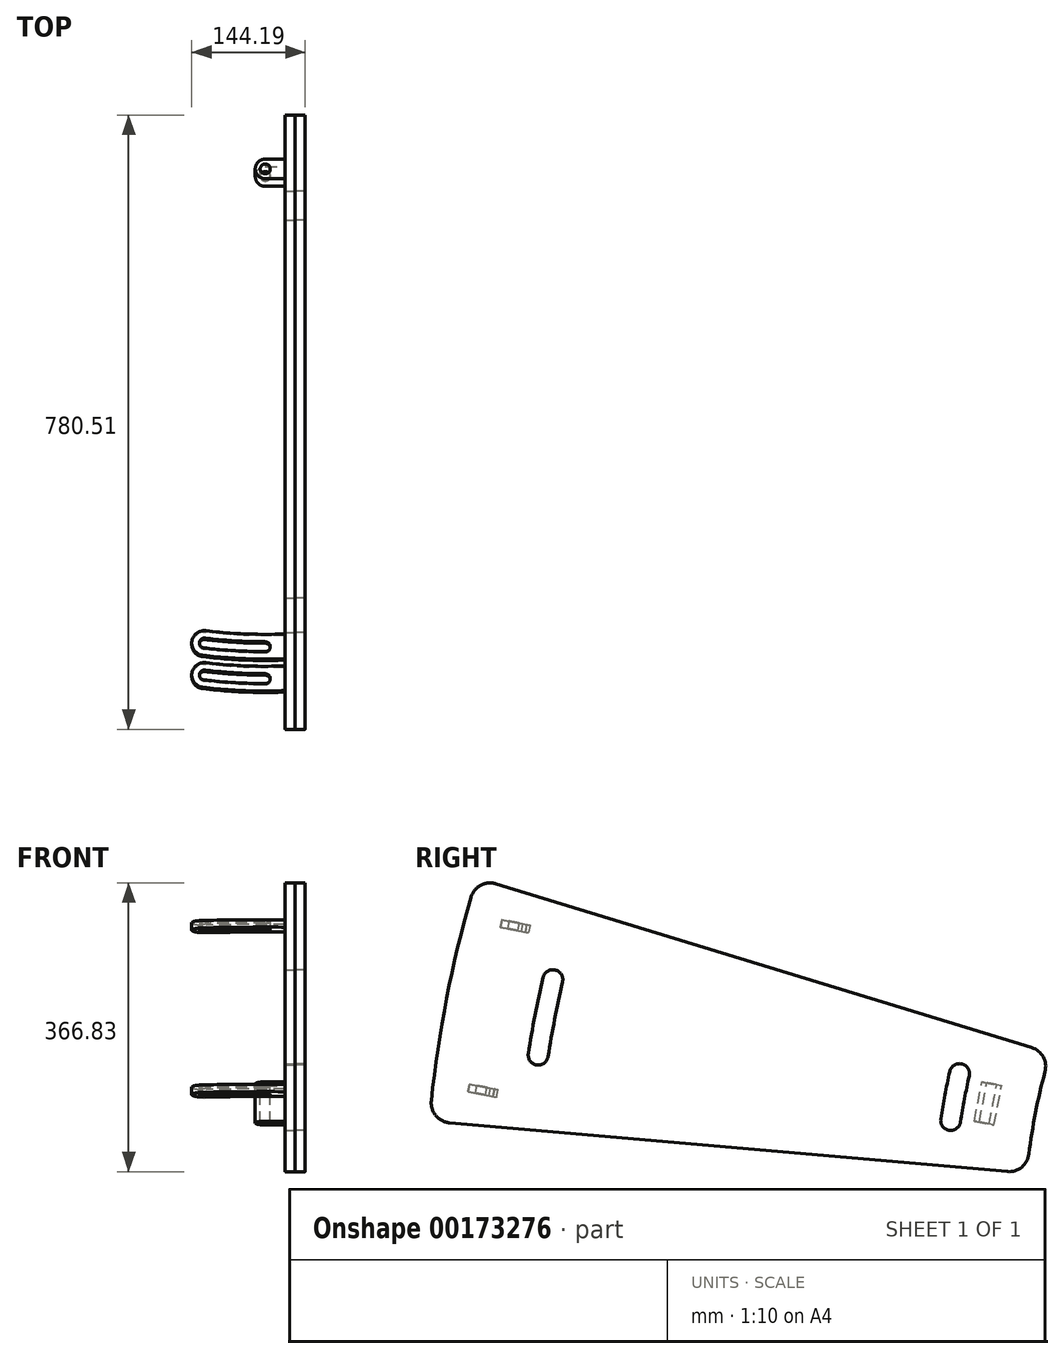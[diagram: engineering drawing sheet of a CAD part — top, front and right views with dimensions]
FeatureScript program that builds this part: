
annotation { "Feature Type Name" : "Feature", "Feature Type Description" : "" }
export const myFeature = defineFeature(function(context is Context, id is Id, definition is map)
    precondition{}
    {
        {
            var Q0;
            Q0=qCreatedBy(makeId("Right.planeOp"),FACE);
            var sketch = newSketch(context, id + "F0", { "sketchPlane" : qUnion([Q0])});
            skArc(sketch, "E0", {"start": v(-736.01, 197.3) * mm, "mid": v(-748, 145.4) * mm, "end": v(-756.33, 92.77) * mm});
            skLineSegment(sketch, "E1", {"start": v(0, 0) * mm, "end": v(-6.79, 0) * mm, "construction": true});
            skLineSegment(sketch, "E2", {"start": v(0, 0) * mm, "end": v(-1486.5, 288.95) * mm, "construction": true});
            skArc(sketch, "E3", {"start": v(-1465.3, 418.87) * mm, "mid": v(-1496, 290.8) * mm, "end": v(-1515.52, 160.55) * mm});
            skLineSegment(sketch, "E4", {"start": v(22.77, 0) * mm, "end": v(-18.63, 3.62) * mm});
            skArc(sketch, "E5", {"start": v(-844.59, 194.99) * mm, "mid": v(-850.72, 165.37) * mm, "end": v(-855.84, 135.55) * mm, "construction": true});
            skArc(sketch, "E6", {"start": v(-1361.2, 314.26) * mm, "mid": v(-1371.33, 266.56) * mm, "end": v(-1379.8, 218.54) * mm, "construction": true});
            skLineSegment(sketch, "E7.MirrorCS", {"start": v(21.1, -8.53) * mm, "end": v(-18.63, 3.62) * mm});
            skLineSegment(sketch, "E8.trimOffspring", {"start": v(-753.12, 228.18) * mm, "end": v(-1433.46, 436.18) * mm});
            skLineSegment(sketch, "E9.trimOffspring", {"start": v(-783.76, 70.56) * mm, "end": v(-1492.48, 132.57) * mm});
            skLineSegment(sketch, "E10.trimOffspring", {"start": v(-762, 0) * mm, "end": v(-1563.5, 0) * mm, "construction": true});
            skPoint(sketch, "E11.orphan", {"position": v(-1640.89, 499.6) * mm});
            skLineSegment(sketch, "E12", {"start": v(0, 0) * mm, "end": v(-1555.73, 246.4) * mm, "construction": true});
            skLineSegment(sketch, "E13", {"start": v(0, 0) * mm, "end": v(0, 0) * mm});
            skLineSegment(sketch, "E14.MirrorCS", {"start": v(0, 0) * mm, "end": v(-1534.75, 354.33) * mm, "construction": true});
            skArc(sketch, "E15.trimOffspring", {"start": v(-862.85, 77.48) * mm, "mid": v(-865.39, 38.78) * mm, "end": v(-866.23, 0) * mm, "construction": true});
            skArc(sketch, "E16.trimOffspring", {"start": v(-1391.5, 123.73) * mm, "mid": v(1371.33, -266.56) * mm, "end": v(-1336.54, 406.55) * mm, "construction": true});
            skArc(sketch, "E17.0.startCap", {"start": v(-1373.57, 317.11) * mm, "mid": v(-1358.34, 326.63) * mm, "end": v(-1348.82, 311.4) * mm});
            skArc(sketch, "E17.0.endCap", {"start": v(-1367.26, 216.55) * mm, "mid": v(-1381.79, 206) * mm, "end": v(-1392.34, 220.53) * mm});
            skArc(sketch, "E17.0.left", {"start": v(-1348.82, 311.4) * mm, "mid": v(-1358.87, 264.14) * mm, "end": v(-1367.26, 216.55) * mm});
            skArc(sketch, "E17.0.right", {"start": v(-1373.57, 317.11) * mm, "mid": v(-1383.8, 268.98) * mm, "end": v(-1392.34, 220.53) * mm});
            skArc(sketch, "E18.0.startCap", {"start": v(-856.98, 197.77) * mm, "mid": v(-841.8, 207.38) * mm, "end": v(-832.2, 192.2) * mm});
            skArc(sketch, "E18.0.endCap", {"start": v(-843.29, 133.62) * mm, "mid": v(-857.78, 123) * mm, "end": v(-868.4, 137.49) * mm});
            skArc(sketch, "E18.0.left", {"start": v(-832.2, 192.2) * mm, "mid": v(-838.24, 163) * mm, "end": v(-843.29, 133.62) * mm});
            skArc(sketch, "E18.0.right", {"start": v(-856.98, 197.77) * mm, "mid": v(-863.2, 167.73) * mm, "end": v(-868.4, 137.49) * mm});
            skPoint(sketch, "E19.visualSharp", {"position": v(-1457.99, 443.68) * mm});
            skArc(sketch, "E19.filletArc", {"start": v(-1433.46, 436.18) * mm, "mid": v(-1453.01, 434.2) * mm, "end": v(-1465.3, 418.87) * mm});
            skPoint(sketch, "E20.visualSharp", {"position": v(-729.28, 220.89) * mm});
            skArc(sketch, "E20.filletArc", {"start": v(-736.01, 197.3) * mm, "mid": v(-738.33, 216.2) * mm, "end": v(-753.12, 228.18) * mm});
            skPoint(sketch, "E21.visualSharp", {"position": v(-758.92, 68.39) * mm});
            skArc(sketch, "E21.filletArc", {"start": v(-783.76, 70.56) * mm, "mid": v(-765.56, 76.13) * mm, "end": v(-756.33, 92.77) * mm});
            skPoint(sketch, "E22.newPointA", {"position": v(-1708.56, 151.47) * mm});
            skArc(sketch, "E22.filletArc", {"start": v(-1515.52, 160.55) * mm, "mid": v(-1509.87, 141.72) * mm, "end": v(-1492.48, 132.57) * mm});
            skSolve(sketch);
        }
        {
            var Q0;
            Q0=makeQuery(id+"F0.imprint","IMPRINT",FACE,{"disambiguationData":[TD([[makeQuery(id+"F0.imprint","IMPRINT",EDGE,{"derivedFrom":sQuery(id+"F0.wireOp",EDGE,"E0")}),-1.0]])]});
            var Q1;
            Q1=makeQuery(id+"F0.imprint","IMPRINT",FACE,{"disambiguationData":[TD([[makeQuery(id+"F0.imprint","IMPRINT",EDGE,{"derivedFrom":sQuery(id+"F0.wireOp",EDGE,"E17.0.startCap")}),-1.0]])]});
            var Q2;
            Q2=makeQuery(id+"F0.imprint","IMPRINT",FACE,{"disambiguationData":[TD([[makeQuery(id+"F0.imprint","IMPRINT",EDGE,{"derivedFrom":sQuery(id+"F0.wireOp",EDGE,"E18.0.startCap")}),-1.0]])]});
            extrude(context, id + "F1", {"entities" : qUnion([Q0, Q1, Q2]), "oppositeDirection" : true, "depth" : 12.7 * mm});
        }
        {
            var Q0;
            Q0=makeQuery(id+"F0.imprint","IMPRINT",FACE,{"disambiguationData":[TD([[makeQuery(id+"F0.imprint","IMPRINT",EDGE,{"derivedFrom":sQuery(id+"F0.wireOp",EDGE,"E17.0.startCap")}),-1.0]])]});
            var Q1;
            Q1=makeQuery(id+"F0.imprint","IMPRINT",FACE,{"disambiguationData":[TD([[makeQuery(id+"F0.imprint","IMPRINT",EDGE,{"derivedFrom":sQuery(id+"F0.wireOp",EDGE,"E18.0.startCap")}),-1.0]])]});
            extrude(context, id + "F2", {"entities" : qUnion([Q0, Q1]), "depth" : 12.7 * mm});
        }
        {
            var Q0;
            Q0=makeQuery(id+"F2.opExtrude","CAP_FACE",FACE,{"disambiguationData":[OSD([sQuery(id+"F0.wireOp",EDGE,"E17.0.startCap"),sQuery(id+"F0.wireOp",EDGE,"E17.0.endCap"),sQuery(id+"F0.wireOp",EDGE,"E17.0.left"),sQuery(id+"F0.wireOp",EDGE,"E17.0.right")])],"isStart":false});
            var sketch = newSketch(context, id + "F3", { "sketchPlane" : qUnion([Q0])});
            skPoint(sketch, "E23", {"position": v(-1361.2, 314.26) * mm});
            skPoint(sketch, "E24", {"position": v(-1379.8, 218.54) * mm});
            skArc(sketch, "E25.0.0", {"start": v(-832.2, 192.2) * mm, "mid": v(-841.8, 207.38) * mm, "end": v(-856.98, 197.77) * mm, "construction": true});
            skArc(sketch, "E25.0.1", {"start": v(-856.98, 197.77) * mm, "mid": v(-863.2, 167.73) * mm, "end": v(-868.4, 137.49) * mm, "construction": true});
            skArc(sketch, "E25.0.2", {"start": v(-868.4, 137.49) * mm, "mid": v(-857.78, 123) * mm, "end": v(-843.29, 133.62) * mm, "construction": true});
            skArc(sketch, "E25.0.3", {"start": v(-843.29, 133.62) * mm, "mid": v(-838.24, 163) * mm, "end": v(-832.2, 192.2) * mm, "construction": true});
            skSolve(sketch);
        }
        {
            var Q0;
            Q0=sQuery(id+"F3.wireOp",VERTEX,"E23");
            var Q1;
            Q1=sQuery(id+"F3.wireOp",VERTEX,"E24");
            var Q2;
            Q2=sQuery(id+"F3.wireOp",VERTEX,"E25.0.0.center");
            var Q3;
            Q3=sQuery(id+"F3.wireOp",VERTEX,"E25.0.2.center");
            var Q4;
            Q4=makeQuery(id+"F1.opExtrude","SWEPT_BODY",BODY,{"disambiguationData":[OSD([sQuery(id+"F0.wireOp",EDGE,"E0"),sQuery(id+"F0.wireOp",EDGE,"E3"),sQuery(id+"F0.wireOp",EDGE,"E8.trimOffspring"),sQuery(id+"F0.wireOp",EDGE,"E9.trimOffspring"),sQuery(id+"F0.wireOp",EDGE,"E19.filletArc"),sQuery(id+"F0.wireOp",EDGE,"E20.filletArc"),sQuery(id+"F0.wireOp",EDGE,"E21.filletArc"),sQuery(id+"F0.wireOp",EDGE,"E22.filletArc")])]});
            hole(context, id + "F4", {"style" : HoleStyle.SIMPLE, "endStyle" : HoleEndStyle.THROUGH, "standardTappedOrClearance" : lookupTablePath({ "standard" : "ANSI", "fit" : "Normal (ASME)", "size" : "5/8", "type" : "Clearance" }), "standardBlindInLast" : lookupTablePath({ "fit" : "Free", "standard" : "ANSI", "size" : "5/8", "type" : "Clearance" }), "holeDiameter" : 16.67 * mm, "locations" : qUnion([Q0, Q1, Q2, Q3]), "scope" : qUnion([Q4]), "isTappedThrough" : true});
        }
        {
            var Q0;
            Q0=makeQuery(id+"F1.opExtrude","SWEPT_FACE",FACE,{"disambiguationData":[OSD([sQuery(id+"F0.wireOp",EDGE,"E9.trimOffspring")])]});
            var Q1;
            Q1=makeQuery(id+"F1.opExtrude","SWEPT_FACE",FACE,{"disambiguationData":[OSD([sQuery(id+"F0.wireOp",EDGE,"E8.trimOffspring")])]});
            cPlane(context, id + "F5", {"entities" : qUnion([Q0, Q1]), "cplaneType" : CPlaneType.MID_PLANE, "offset" : 25.4 * mm, "width" : 152.4 * mm, "height" : 152.4 * mm});
        }
        {
            var Q0;
            Q0=qCreatedBy(id+"F5.planeOp",FACE);
            var sketch = newSketch(context, id + "F6", { "sketchPlane" : qUnion([Q0])});
            skLineSegment(sketch, "E26.0", {"start": v(-12.7, 782.82) * mm, "end": v(-12.7, 1490.35) * mm, "construction": true});
            skLineSegment(sketch, "E27", {"start": v(0, 760.08) * mm, "end": v(-12.7, 760.08) * mm, "construction": true});
            skLineSegment(sketch, "E28", {"start": v(-12.7, 760.08) * mm, "end": v(-65.49, 760.08) * mm, "construction": true});
            skLineSegment(sketch, "E29.0", {"start": v(-12.7, 823.58) * mm, "end": v(-38.1, 823.58) * mm, "construction": true});
            skCircle(sketch, "E30", {"center": v(-38.1, 823.58) * mm, "radius": 6.35 * mm});
            skCircle(sketch, "E31", {"center": v(-38.1, 823.58) * mm, "radius": 12.7 * mm});
            skLineSegment(sketch, "E32", {"start": v(-38.1, 829.93) * mm, "end": v(-38.1, 836.28) * mm});
            skLineSegment(sketch, "E33", {"start": v(-38.1, 836.28) * mm, "end": v(-12.7, 836.28) * mm});
            skLineSegment(sketch, "E34", {"start": v(-38.1, 817.23) * mm, "end": v(-38.1, 810.88) * mm});
            skLineSegment(sketch, "E35", {"start": v(-38.1, 810.88) * mm, "end": v(-12.7, 810.88) * mm});
            skLineSegment(sketch, "E36", {"start": v(-12.7, 810.88) * mm, "end": v(-12.7, 836.28) * mm});
            skSolve(sketch);
        }
        {
            var Q0;
            Q0 = qSketchRegion(id + "F6", true);
            extrude(context, id + "F7", {"entities" : qUnion([Q0]), "operationType" : NewBodyOperationType.ADD, "endBound" : BoundingType.SYMMETRIC, "depth" : 50.8 * mm});
        }
        {
            var Q0;
            Q0=qCreatedBy(id+"F5.planeOp",FACE);
            cPlane(context, id + "F8", {"entities" : qUnion([Q0]), "cplaneType" : CPlaneType.OFFSET, "offset" : 101.6 * mm, "width" : 152.4 * mm, "height" : 152.4 * mm});
        }
        {
            var Q0;
            Q0=qCreatedBy(id+"F8.planeOp",FACE);
            var sketch = newSketch(context, id + "F9", { "sketchPlane" : qUnion([Q0])});
            skLineSegment(sketch, "E37.0.0", {"start": v(-12.7, 836.28) * mm, "end": v(-38.1, 836.28) * mm, "construction": true});
            skArc(sketch, "E37.0.1", {"start": v(-38.1, 836.28) * mm, "mid": v(-50.8, 823.58) * mm, "end": v(-38.1, 810.88) * mm, "construction": true});
            skLineSegment(sketch, "E37.0.2", {"start": v(-38.1, 810.88) * mm, "end": v(-12.7, 810.88) * mm, "construction": true});
            skLineSegment(sketch, "E37.0.3", {"start": v(-12.7, 810.88) * mm, "end": v(-12.7, 836.28) * mm, "construction": true});
            skLineSegment(sketch, "E38.0", {"start": v(0, 1518.3) * mm, "end": v(0, 1524) * mm, "construction": true});
            skLineSegment(sketch, "E38.3", {"start": v(0, 1490.35) * mm, "end": v(0, 1518.3) * mm, "construction": true});
            skLineSegment(sketch, "E38.4", {"start": v(0, 1383.45) * mm, "end": v(0, 1408.84) * mm, "construction": true});
            skLineSegment(sketch, "E38.5", {"start": v(0, 1518.3) * mm, "end": v(0, 1490.35) * mm, "construction": true});
            skLineSegment(sketch, "E38.6", {"start": v(0, 1408.84) * mm, "end": v(0, 1383.45) * mm, "construction": true});
            skLineSegment(sketch, "E38.10", {"start": v(12.7, 1383.45) * mm, "end": v(12.7, 1408.84) * mm, "construction": true});
            skLineSegment(sketch, "E38.11", {"start": v(-12.7, 1490.35) * mm, "end": v(0, 1490.35) * mm, "construction": true});
            skLineSegment(sketch, "E38.12", {"start": v(-12.7, 1518.3) * mm, "end": v(-12.7, 1490.35) * mm, "construction": true});
            skLineSegment(sketch, "E38.13", {"start": v(-12.7, 782.82) * mm, "end": v(-12.7, 836.28) * mm, "construction": true});
            skLineSegment(sketch, "E38.14", {"start": v(-12.7, 1518.3) * mm, "end": v(-12.7, 1524) * mm, "construction": true});
            skLineSegment(sketch, "E38.15", {"start": v(0, 1389.55) * mm, "end": v(0, -1397) * mm, "construction": true});
            skLineSegment(sketch, "E38.17", {"start": v(12.7, 1408.84) * mm, "end": v(0, 1408.84) * mm, "construction": true});
            skLineSegment(sketch, "E38.18", {"start": v(-12.7, 1518.3) * mm, "end": v(0, 1518.3) * mm, "construction": true});
            skLineSegment(sketch, "E38.19", {"start": v(0, 1518.3) * mm, "end": v(0, 1524) * mm, "construction": true});
            skLineSegment(sketch, "E38.20", {"start": v(-12.7, 1387.82) * mm, "end": v(-12.7, 1404.48) * mm, "construction": true});
            skLineSegment(sketch, "E38.21", {"start": v(12.7, 1401.9) * mm, "end": v(12.7, 1390.4) * mm, "construction": true});
            skLineSegment(sketch, "E38.22", {"start": v(12.7, 1401.9) * mm, "end": v(12.7, 1390.4) * mm, "construction": true});
            skLineSegment(sketch, "E38.23", {"start": v(-12.7, 1490.35) * mm, "end": v(-12.7, 1518.3) * mm, "construction": true});
            skLineSegment(sketch, "E38.24", {"start": v(-12.7, 1387.82) * mm, "end": v(-12.7, 1404.48) * mm, "construction": true});
            skLineSegment(sketch, "E38.25", {"start": v(12.7, 1408.84) * mm, "end": v(12.7, 1383.45) * mm, "construction": true});
            skLineSegment(sketch, "E38.26", {"start": v(-12.7, 1518.3) * mm, "end": v(0, 1518.3) * mm, "construction": true});
            skLineSegment(sketch, "E38.27", {"start": v(-12.7, 782.82) * mm, "end": v(-12.7, 1387.82) * mm, "construction": true});
            skLineSegment(sketch, "E38.29", {"start": v(-12.7, 1490.35) * mm, "end": v(0, 1490.35) * mm, "construction": true});
            skLineSegment(sketch, "E38.30", {"start": v(0, 1518.3) * mm, "end": v(0, 1490.35) * mm, "construction": true});
            skLineSegment(sketch, "E38.31", {"start": v(12.7, 1383.46) * mm, "end": v(0, 1383.46) * mm, "construction": true});
            skLineSegment(sketch, "E38.32", {"start": v(12.7, 1408.84) * mm, "end": v(12.7, 1409.7) * mm, "construction": true});
            skLineSegment(sketch, "E38.33", {"start": v(0, 1396.15) * mm, "end": v(0, 1397) * mm, "construction": true});
            skLineSegment(sketch, "E38.34", {"start": v(0, 1383.46) * mm, "end": v(0, 1384.3) * mm, "construction": true});
            skLineSegment(sketch, "E38.35", {"start": v(0, 1408.84) * mm, "end": v(0, 1409.7) * mm, "construction": true});
            skLineSegment(sketch, "E38.37", {"start": v(12.7, 1383.46) * mm, "end": v(0, 1383.46) * mm, "construction": true});
            skLineSegment(sketch, "E38.38", {"start": v(12.7, 1408.84) * mm, "end": v(0, 1408.84) * mm, "construction": true});
            skLineSegment(sketch, "E38.39", {"start": v(0, 1490.35) * mm, "end": v(0, 1518.3) * mm, "construction": true});
            skLineSegment(sketch, "E38.40", {"start": v(12.7, 1383.46) * mm, "end": v(12.7, 1384.3) * mm, "construction": true});
            skLineSegment(sketch, "E38.41", {"start": v(0, 1383.45) * mm, "end": v(0, 1408.84) * mm, "construction": true});
            skLineSegment(sketch, "E38.42", {"start": v(0, 1408.84) * mm, "end": v(0, 1409.7) * mm, "construction": true});
            skLineSegment(sketch, "E38.43", {"start": v(0, 1383.46) * mm, "end": v(0, 1384.3) * mm, "construction": true});
            skLineSegment(sketch, "E38.44", {"start": v(0, 1408.84) * mm, "end": v(0, 1383.45) * mm, "construction": true});
            skArc(sketch, "E39", {"start": v(0, 189.72) * mm, "mid": v(596.87, 829.93) * mm, "end": v(-12.7, 1458.07) * mm, "construction": true});
            skLineSegment(sketch, "E40", {"start": v(-38.1, 823.58) * mm, "end": v(-38.1, 1674.01) * mm, "construction": true});
            skLineSegment(sketch, "E41", {"start": v(-38.1, 823.58) * mm, "end": v(-115.49, 1453.84) * mm, "construction": true});
            skArc(sketch, "E42", {"start": v(-38.1, 1452.23) * mm, "mid": v(-31.75, 1458.58) * mm, "end": v(-38.1, 1464.93) * mm});
            skArc(sketch, "E43", {"start": v(-116.26, 1460.14) * mm, "mid": v(-121.79, 1453.07) * mm, "end": v(-114.71, 1447.54) * mm});
            skArc(sketch, "E44.trimOffspring", {"start": v(-31.75, 1458.54) * mm, "mid": v(-76.87, 1457.4) * mm, "end": v(-121.79, 1453.04) * mm, "construction": true});
            skArc(sketch, "E45.0", {"start": v(-38.1, 1464.93) * mm, "mid": v(-77.25, 1463.73) * mm, "end": v(-116.26, 1460.14) * mm});
            skArc(sketch, "E46.0", {"start": v(-38.1, 1452.23) * mm, "mid": v(-76.48, 1451.05) * mm, "end": v(-114.71, 1447.54) * mm});
            skLineSegment(sketch, "E47.0.0", {"start": v(0, 782.82) * mm, "end": v(0, 1409.7) * mm});
            skLineSegment(sketch, "E47.0.1", {"start": v(0, 1490.35) * mm, "end": v(-12.7, 1490.35) * mm});
            skLineSegment(sketch, "E47.0.2", {"start": v(-12.7, 1474.08) * mm, "end": v(-12.7, 1458.07) * mm});
            skLineSegment(sketch, "E47.0.3", {"start": v(-12.7, 782.82) * mm, "end": v(0, 782.82) * mm});
            skArc(sketch, "E48.0", {"start": v(-117.44, 1469.72) * mm, "mid": v(-131.37, 1451.9) * mm, "end": v(-113.54, 1437.96) * mm});
            skArc(sketch, "E49.0", {"start": v(-12.7, 1442.05) * mm, "mid": v(-63.2, 1442.06) * mm, "end": v(-113.54, 1437.96) * mm});
            skArc(sketch, "E50.0", {"start": v(-12.7, 1474.08) * mm, "mid": v(-68.4, 1473.87) * mm, "end": v(-123.9, 1468.9) * mm});
            skPoint(sketch, "E38.8.start.orphan", {"position": v(0, 748) * mm});
            skLineSegment(sketch, "E51.trimOffspring", {"start": v(-12.7, 1442.05) * mm, "end": v(-12.7, 1458.07) * mm, "construction": true});
            skLineSegment(sketch, "E52.trimOffspring", {"start": v(-12.7, 1442.05) * mm, "end": v(-12.7, 1474.08) * mm});
            skLineSegment(sketch, "E53.trimOffspring", {"start": v(-12.7, 1404.48) * mm, "end": v(-12.7, 782.82) * mm});
            skSolve(sketch);
        }
        {
            var Q0;
            Q0 = qSketchRegion(id + "F9", true);
            extrude(context, id + "F10", {"entities" : qUnion([Q0]), "depth" : 9.65 * mm});
        }
        {
            var Q0;
            Q0=makeQuery(id+"F10.opExtrude","SWEPT_BODY",BODY,{"disambiguationData":[OSD([sQuery(id+"F9.wireOp",EDGE,"E42"),sQuery(id+"F9.wireOp",EDGE,"E43"),sQuery(id+"F9.wireOp",EDGE,"E45.0"),sQuery(id+"F9.wireOp",EDGE,"E46.0"),sQuery(id+"F9.wireOp",EDGE,"E48.0"),sQuery(id+"F9.wireOp",EDGE,"E49.0"),sQuery(id+"F9.wireOp",EDGE,"E50.0"),sQuery(id+"F9.wireOp",EDGE,"E52.trimOffspring")])]});
            var Q1;
            Q1=qCreatedBy(id+"F5.planeOp",FACE);
            mirror(context, id + "F11", {"entities" : qUnion([Q0]), "mirrorPlane" : qUnion([Q1])});
        }
        {
            var Q0;
            Q0=makeQuery(id+"F2.opExtrude","CAP_FACE",FACE,{"disambiguationData":[OSD([sQuery(id+"F0.wireOp",EDGE,"E18.0.startCap"),sQuery(id+"F0.wireOp",EDGE,"E18.0.endCap"),sQuery(id+"F0.wireOp",EDGE,"E18.0.left"),sQuery(id+"F0.wireOp",EDGE,"E18.0.right")])],"isStart":false});
            var sketch = newSketch(context, id + "F12", { "sketchPlane" : qUnion([Q0])});
            skArc(sketch, "E54.0.0", {"start": v(-832.2, 192.2) * mm, "mid": v(-841.8, 207.38) * mm, "end": v(-856.98, 197.77) * mm, "construction": true});
            skArc(sketch, "E54.0.1", {"start": v(-856.98, 197.77) * mm, "mid": v(-863.2, 167.73) * mm, "end": v(-868.4, 137.49) * mm, "construction": true});
            skArc(sketch, "E54.0.2", {"start": v(-868.4, 137.49) * mm, "mid": v(-857.78, 123) * mm, "end": v(-843.29, 133.62) * mm, "construction": true});
            skArc(sketch, "E54.0.3", {"start": v(-843.29, 133.62) * mm, "mid": v(-838.24, 163) * mm, "end": v(-832.2, 192.2) * mm, "construction": true});
            skSolve(sketch);
        }
        {
            var Q0;
            Q0=sQuery(id+"F12.wireOp",VERTEX,"E54.0.0.center");
            var Q1;
            Q1=sQuery(id+"F12.wireOp",VERTEX,"E54.0.2.center");
            var Q2;
            Q2=makeQuery(id+"F2.opExtrude","SWEPT_BODY",BODY,{"disambiguationData":[OSD([sQuery(id+"F0.wireOp",EDGE,"E18.0.startCap"),sQuery(id+"F0.wireOp",EDGE,"E18.0.endCap"),sQuery(id+"F0.wireOp",EDGE,"E18.0.left"),sQuery(id+"F0.wireOp",EDGE,"E18.0.right")])]});
            hole(context, id + "F13", {"style" : HoleStyle.SIMPLE, "endStyle" : HoleEndStyle.THROUGH, "standardTappedOrClearance" : lookupTablePath({ "standard" : "ANSI", "fit" : "Normal (ASME)", "size" : "5/8", "type" : "Clearance" }), "standardBlindInLast" : lookupTablePath({ "fit" : "Free", "standard" : "ANSI", "size" : "5/8", "type" : "Clearance" }), "holeDiameter" : 16.67 * mm, "locations" : qUnion([Q0, Q1]), "scope" : qUnion([Q2]), "isTappedThrough" : true});
        }
        {
            var Q0;
            Q0=makeQuery(id+"F2.opExtrude","CAP_FACE",FACE,{"disambiguationData":[OSD([sQuery(id+"F0.wireOp",EDGE,"E17.0.startCap"),sQuery(id+"F0.wireOp",EDGE,"E17.0.endCap"),sQuery(id+"F0.wireOp",EDGE,"E17.0.left"),sQuery(id+"F0.wireOp",EDGE,"E17.0.right")])],"isStart":false});
            var sketch = newSketch(context, id + "F14", { "sketchPlane" : qUnion([Q0])});
            skArc(sketch, "E55.0.0", {"start": v(-1348.82, 311.4) * mm, "mid": v(-1358.34, 326.63) * mm, "end": v(-1373.57, 317.11) * mm, "construction": true});
            skArc(sketch, "E55.0.1", {"start": v(-1373.57, 317.11) * mm, "mid": v(-1383.8, 268.98) * mm, "end": v(-1392.34, 220.53) * mm, "construction": true});
            skArc(sketch, "E55.0.2", {"start": v(-1392.34, 220.53) * mm, "mid": v(-1381.79, 206) * mm, "end": v(-1367.26, 216.55) * mm, "construction": true});
            skArc(sketch, "E55.0.3", {"start": v(-1367.26, 216.55) * mm, "mid": v(-1358.87, 264.14) * mm, "end": v(-1348.82, 311.4) * mm, "construction": true});
            skSolve(sketch);
        }
        {
            var Q0;
            Q0=sQuery(id+"F14.wireOp",VERTEX,"E55.0.0.center");
            var Q1;
            Q1=sQuery(id+"F14.wireOp",VERTEX,"E55.0.2.center");
            var Q2;
            Q2=makeQuery(id+"F2.opExtrude","SWEPT_BODY",BODY,{"disambiguationData":[OSD([sQuery(id+"F0.wireOp",EDGE,"E17.0.startCap"),sQuery(id+"F0.wireOp",EDGE,"E17.0.endCap"),sQuery(id+"F0.wireOp",EDGE,"E17.0.left"),sQuery(id+"F0.wireOp",EDGE,"E17.0.right")])]});
            hole(context, id + "F15", {"style" : HoleStyle.SIMPLE, "endStyle" : HoleEndStyle.THROUGH, "standardTappedOrClearance" : lookupTablePath({ "standard" : "ANSI", "fit" : "Normal (ASME)", "size" : "5/8", "type" : "Clearance" }), "standardBlindInLast" : lookupTablePath({ "fit" : "Free", "standard" : "ANSI", "size" : "5/8", "type" : "Clearance" }), "holeDiameter" : 16.67 * mm, "locations" : qUnion([Q0, Q1]), "scope" : qUnion([Q2]), "isTappedThrough" : true});
        }
    });
